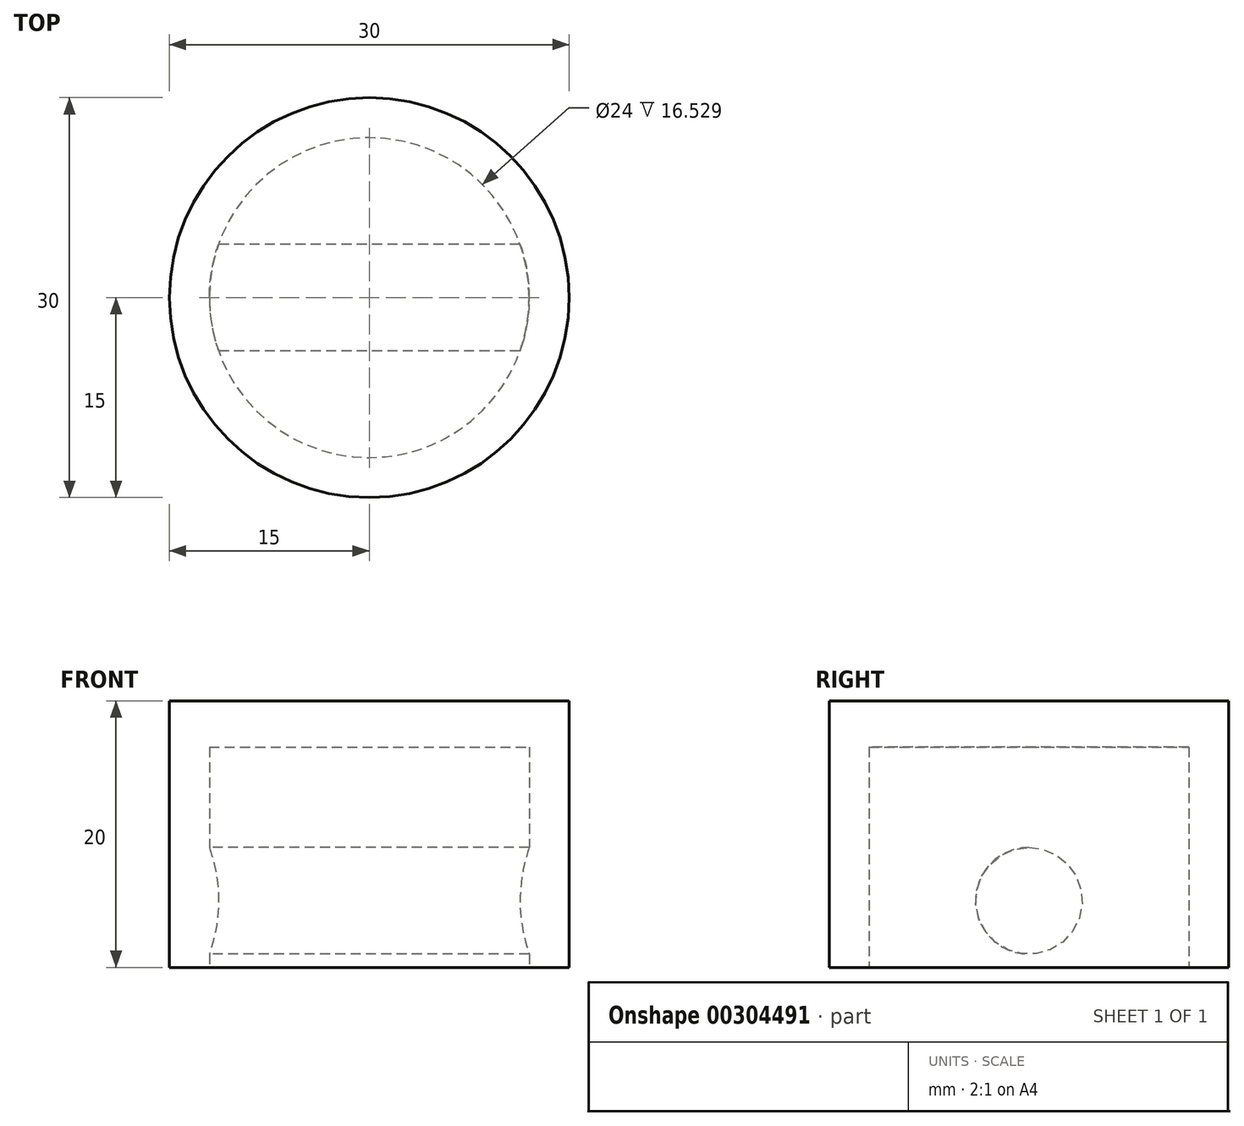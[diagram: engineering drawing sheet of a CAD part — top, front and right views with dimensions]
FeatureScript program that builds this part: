
annotation { "Feature Type Name" : "Feature", "Feature Type Description" : "" }
export const myFeature = defineFeature(function(context is Context, id is Id, definition is map)
    precondition{}
    {
        {
            var Q0;
            Q0=qCreatedBy(makeId("Right.planeOp"),FACE);
            var sketch = newSketch(context, id + "F0", { "sketchPlane" : qUnion([Q0])});
            skLineSegment(sketch, "E0", {"start": v(0, 0) * mm, "end": v(0, 20) * mm, "construction": true});
            skLineSegment(sketch, "E1", {"start": v(0, 20) * mm, "end": v(15, 20) * mm});
            skLineSegment(sketch, "E2", {"start": v(15, 20) * mm, "end": v(15, 0) * mm});
            skLineSegment(sketch, "E3", {"start": v(15, 0) * mm, "end": v(12, 0) * mm});
            skLineSegment(sketch, "E4", {"start": v(12, 0) * mm, "end": v(12, 16.53) * mm});
            skLineSegment(sketch, "E5", {"start": v(12, 16.53) * mm, "end": v(0, 16.53) * mm});
            skLineSegment(sketch, "E6", {"start": v(0, 16.53) * mm, "end": v(0, 20) * mm});
            skCircle(sketch, "E7", {"center": v(0, 5) * mm, "radius": 4 * mm});
            skSolve(sketch);
        }
        {
            var Q0;
            Q0=makeQuery(id+"F0.imprint","IMPRINT",FACE,{"disambiguationData":[TD([[makeQuery(id+"F0.imprint","IMPRINT",EDGE,{"derivedFrom":sQuery(id+"F0.wireOp",EDGE,"E1")}),-1.0]])]});
            var Q1;
            Q1=sQuery(id+"F0.wireOp",EDGE,"E0");
            revolve(context, id + "F1", {"entities" : qUnion([Q0]), "axis" : qUnion([Q1]), "revolveType" : RevolveType.FULL});
        }
        {
            var Q0;
            Q0=makeQuery(id+"F0.imprint","IMPRINT",FACE,{"disambiguationData":[TD([[makeQuery(id+"F0.imprint","IMPRINT",EDGE,{"derivedFrom":sQuery(id+"F0.wireOp",EDGE,"E7")}),1.0]])]});
            extrude(context, id + "F2", {"entities" : qUnion([Q0]), "operationType" : NewBodyOperationType.ADD, "depth" : 25 * mm, "symmetric" : true});
        }
    });
